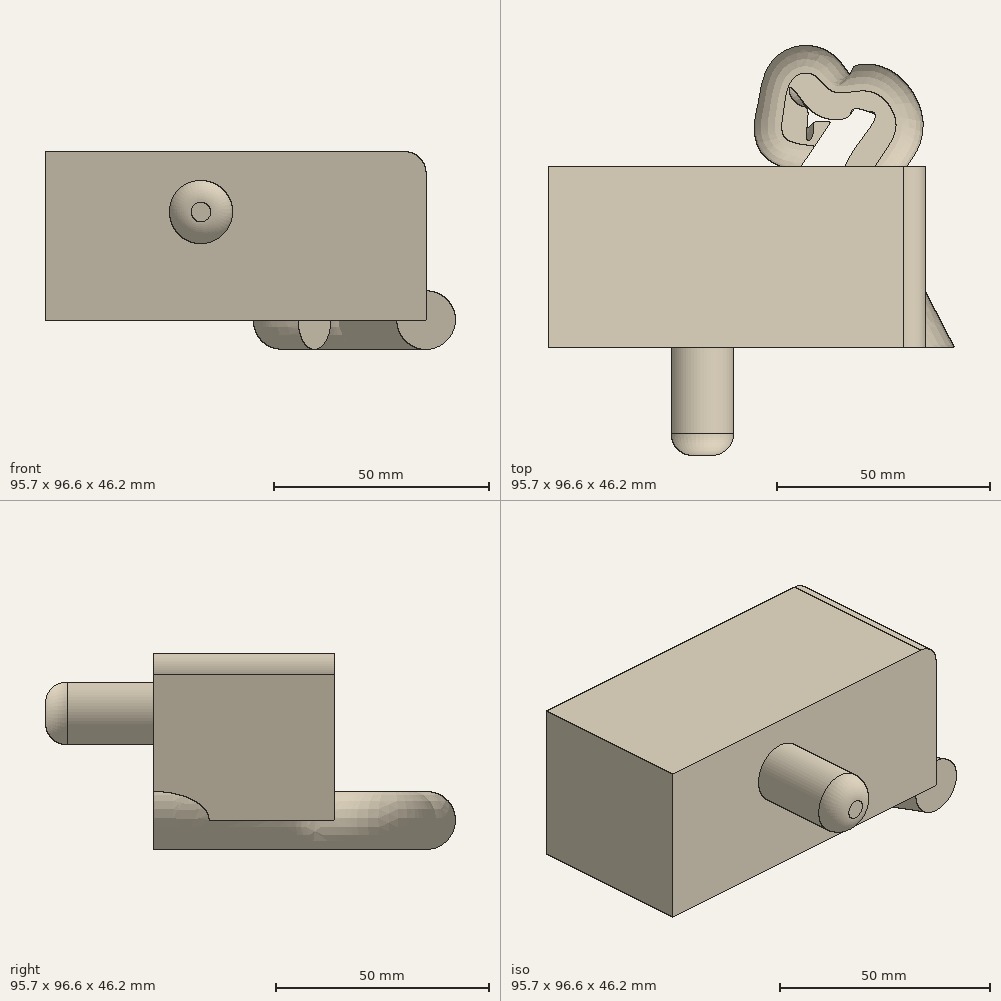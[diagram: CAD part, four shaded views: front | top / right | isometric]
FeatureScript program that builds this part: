
annotation { "Feature Type Name" : "Feature", "Feature Type Description" : "" }
export const myFeature = defineFeature(function(context is Context, id is Id, definition is map)
    precondition{}
    {
        {
            var Q0;
            Q0=qCreatedBy(makeId("Top.planeOp"),FACE);
            var sketch = newSketch(context, id + "F0", { "sketchPlane" : qUnion([Q0])});
            skLineSegment(sketch, "E0.bottom", {"start": v(-36.31, 18.6) * mm, "end": v(52.52, 18.6) * mm});
            skLineSegment(sketch, "E0.top", {"start": v(-36.31, -24) * mm, "end": v(52.52, -24) * mm});
            skLineSegment(sketch, "E0.left", {"start": v(-36.31, 18.6) * mm, "end": v(-36.31, -24) * mm});
            skLineSegment(sketch, "E0.right", {"start": v(52.52, 18.6) * mm, "end": v(52.52, -24) * mm});
            skSolve(sketch);
        }
        {
            var Q0;
            Q0 = qSketchRegion(id + "F0", true);
            extrude(context, id + "F1", {"entities" : qUnion([Q0]), "depth" : 39.37 * mm, "offsetDistance" : 25.4 * mm});
        }
        {
            var Q0;
            Q0=makeQuery(id+"F1.opExtrude","SWEPT_FACE",FACE,{"disambiguationData":[OSD([sQuery(id+"F0.wireOp",EDGE,"E0.top")])]});
            var sketch = newSketch(context, id + "F2", { "sketchPlane" : qUnion([Q0])});
            skCircle(sketch, "E1", {"center": v(0, 25.21) * mm, "radius": 7.38 * mm});
            skSolve(sketch);
        }
        {
            var Q0;
            Q0 = qSketchRegion(id + "F2", true);
            extrude(context, id + "F3", {"entities" : qUnion([Q0]), "operationType" : NewBodyOperationType.ADD, "depth" : 25.4 * mm, "offsetDistance" : 25.4 * mm});
        }
        {
            var Q0;
            Q0=makeQuery(id+"F1.opExtrude","CAP_EDGE",EDGE,{"disambiguationData":[OSD([sQuery(id+"F0.wireOp",EDGE,"E0.right")])],"isStart":false});
            fillet(context, id + "F4", {"entities" : qUnion([Q0]), "radius" : 5.08 * mm, "tangentPropagation" : true, "allowEdgeOverflow" : false});
        }
        {
            var Q0;
            Q0=makeQuery(id+"F3.opExtrude","CAP_EDGE",EDGE,{"disambiguationData":[OSD([sQuery(id+"F2.wireOp",EDGE,"E1")])],"isStart":false});
            fillet(context, id + "F5", {"entities" : qUnion([Q0]), "radius" : 5.08 * mm, "tangentPropagation" : true, "allowEdgeOverflow" : false});
        }
        {
            var Q0;
            Q0=makeQuery(id+"F1.opExtrude","SWEPT_FACE",FACE,{"disambiguationData":[OSD([sQuery(id+"F0.wireOp",EDGE,"E0.top")])]});
            var sketch = newSketch(context, id + "F6", { "sketchPlane" : qUnion([Q0])});
            skCircle(sketch, "E2", {"center": v(52.52, 0) * mm, "radius": 6.85 * mm});
            skSolve(sketch);
        }
        {
            var Q0;
            Q0=qCreatedBy(makeId("Top.planeOp"),FACE);
            var sketch = newSketch(context, id + "F7", { "sketchPlane" : qUnion([Q0])});
            skFitSpline(sketch, "E3", {"points": [v(52.7, -24.03) * mm, v(46.97, -13) * mm, v(38.8, 13.63) * mm, v(45.7, 27.64) * mm, v(39.86, 36.34) * mm, v(31.05, 36.34) * mm, v(26.17, 40.37) * mm, v(21.4, 39.52) * mm, v(18.85, 31.46) * mm, v(19.27, 25.41) * mm, v(26.38, 23.29) * mm], "startDerivative": vector(-43.17, 82.76) * mm, "endDerivative": vector(103.16, -11.75) * mm});
            skSolve(sketch);
        }
        {
            var Q0;
            {var subQ0=sQuery(id+"F6.wireOp",EDGE,"E2");var subQ1=sQuery(id+"F0.wireOp",EDGE,"E0.top");var subQ2=makeQuery(id+"F1.opExtrude","CAP_EDGE",EDGE,{"disambiguationData":[OSD([subQ1])],"isStart":true});var subQ3=makeQuery(id+"F6.imprint","INTERSECT",VERTEX,{"derivedFrom":[subQ2,subQ0]});Q0=makeQuery(id+"F6.imprint","IMPRINT",FACE,{"disambiguationData":[TD([[makeQuery(id+"F6.imprint","IMPRINT",EDGE,{"disambiguationData":[TD([[subQ3,-1.0]])],"derivedFrom":subQ0}),1.0]])]});}
            var Q1;
            Q1=sQuery(id+"F7.wireOp",EDGE,"E3");
            sweep(context, id + "F8", {"operationType" : NewBodyOperationType.ADD, "profiles" : qUnion([Q0]), "path" : qUnion([Q1])});
        }
    });
